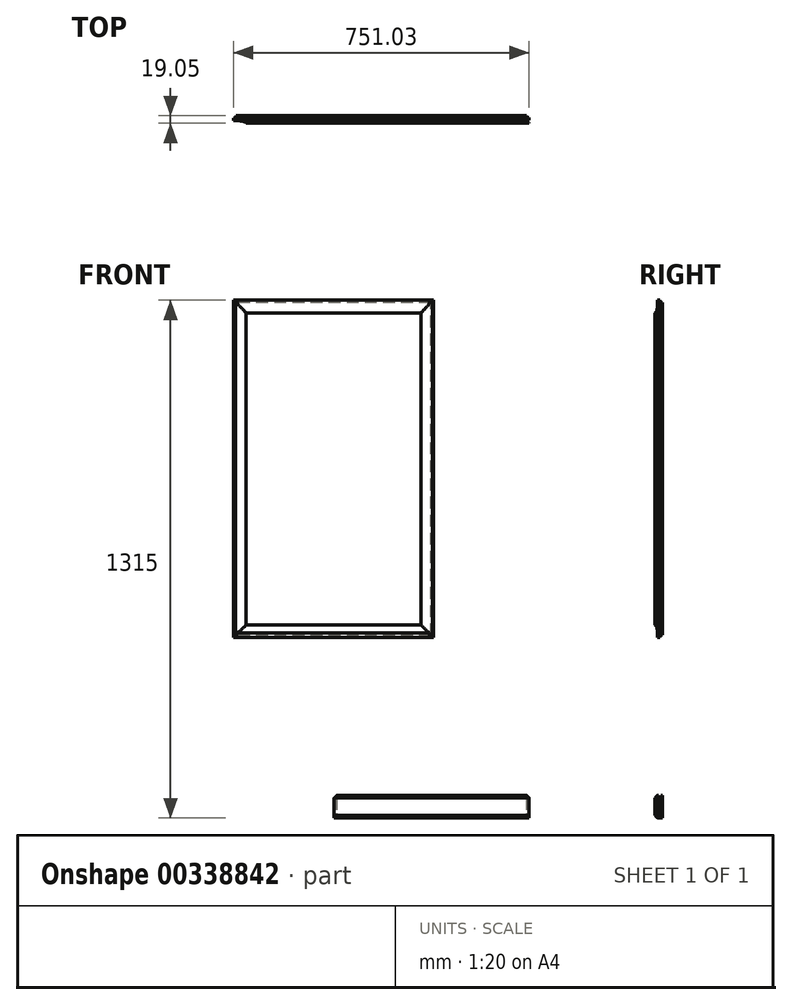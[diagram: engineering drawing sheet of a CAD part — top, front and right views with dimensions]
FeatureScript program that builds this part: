
annotation { "Feature Type Name" : "Feature", "Feature Type Description" : "" }
export const myFeature = defineFeature(function(context is Context, id is Id, definition is map)
    precondition{}
    {
        {
            var Q0;
            Q0=qCreatedBy(makeId("Front.planeOp"),FACE);
            var sketch = newSketch(context, id + "F0", { "sketchPlane" : qUnion([Q0])});
            skLineSegment(sketch, "E0.bottom", {"start": v(-252.27, 59.22) * mm, "end": v(243.03, 59.22) * mm});
            skLineSegment(sketch, "E0.top", {"start": v(-252.27, 2.07) * mm, "end": v(243.03, 2.07) * mm});
            skLineSegment(sketch, "E0.left", {"start": v(-252.27, 59.22) * mm, "end": v(-252.27, 2.07) * mm});
            skLineSegment(sketch, "E0.right", {"start": v(243.03, 59.22) * mm, "end": v(243.03, 2.07) * mm});
            skSolve(sketch);
        }
        {
            var Q0;
            Q0 = qSketchRegion(id + "F0", true);
            extrude(context, id + "F1", {"entities" : qUnion([Q0]), "depth" : 19.05 * mm});
        }
        {
            var Q0;
            Q0=makeQuery(id+"F1.opExtrude","SWEPT_FACE",FACE,{"disambiguationData":[OSD([sQuery(id+"F0.wireOp",EDGE,"E0.top")])]});
            var sketch = newSketch(context, id + "F2", { "sketchPlane" : qUnion([Q0])});
            skLineSegment(sketch, "E1.0", {"start": v(-252.27, 17.46) * mm, "end": v(243.03, 17.46) * mm, "construction": true});
            skLineSegment(sketch, "E2.0", {"start": v(-252.27, 11.11) * mm, "end": v(243.03, 11.11) * mm, "construction": true});
            skLineSegment(sketch, "E3.0", {"start": v(-252.27, 4.76) * mm, "end": v(243.03, 4.76) * mm, "construction": true});
            skLineSegment(sketch, "E4.0", {"start": v(236.68, 25.4) * mm, "end": v(236.68, 0) * mm, "construction": true});
            skArc(sketch, "E5", {"start": v(243.03, 17.46) * mm, "mid": v(238.54, 15.6) * mm, "end": v(236.68, 11.11) * mm});
            skLineSegment(sketch, "E6", {"start": v(236.68, 11.11) * mm, "end": v(243.03, 11.11) * mm});
            skLineSegment(sketch, "E7", {"start": v(243.03, 4.76) * mm, "end": v(236.68, 4.76) * mm});
            skLineSegment(sketch, "E8", {"start": v(236.68, 4.76) * mm, "end": v(236.68, 0) * mm});
            skLineSegment(sketch, "E9.0", {"start": v(-245.92, 19.05) * mm, "end": v(-245.92, 0) * mm, "construction": true});
            skArc(sketch, "E10", {"start": v(-245.92, 11.11) * mm, "mid": v(-247.78, 15.6) * mm, "end": v(-252.27, 17.46) * mm});
            skLineSegment(sketch, "E11", {"start": v(-245.92, 11.11) * mm, "end": v(-252.27, 11.11) * mm});
            skLineSegment(sketch, "E12", {"start": v(-252.27, 4.76) * mm, "end": v(-245.92, 4.76) * mm});
            skLineSegment(sketch, "E13", {"start": v(-245.92, 4.76) * mm, "end": v(-245.92, 0) * mm});
            skSolve(sketch);
        }
        {
            var Q0;
            {var subQ0=sQuery(id+"F2.wireOp",EDGE,"E5");Q0=makeQuery(id+"F2.imprint","IMPRINT",FACE,{"disambiguationData":[TD([[makeQuery(id+"F2.imprint","IMPRINT",EDGE,{"derivedFrom":subQ0}),1.0]])]});}
            var Q1;
            {var subQ0=sQuery(id+"F2.wireOp",EDGE,"E7");Q1=makeQuery(id+"F2.imprint","IMPRINT",FACE,{"disambiguationData":[TD([[makeQuery(id+"F2.imprint","IMPRINT",EDGE,{"derivedFrom":subQ0}),1.0]])]});}
            extrude(context, id + "F3", {"entities" : qUnion([Q0, Q1]), "operationType" : NewBodyOperationType.REMOVE, "oppositeDirection" : true, "depth" : 57.15 * mm});
        }
        {
            var Q0;
            {var subQ0=sQuery(id+"F2.wireOp",EDGE,"E10");Q0=makeQuery(id+"F2.imprint","IMPRINT",FACE,{"disambiguationData":[TD([[makeQuery(id+"F2.imprint","IMPRINT",EDGE,{"derivedFrom":subQ0}),1.0]])]});}
            var Q1;
            {var subQ0=sQuery(id+"F2.wireOp",EDGE,"E12");Q1=makeQuery(id+"F2.imprint","IMPRINT",FACE,{"disambiguationData":[TD([[makeQuery(id+"F2.imprint","IMPRINT",EDGE,{"derivedFrom":subQ0}),-1.0]])]});}
            extrude(context, id + "F4", {"entities" : qUnion([Q0, Q1]), "operationType" : NewBodyOperationType.REMOVE, "oppositeDirection" : true, "depth" : 57.15 * mm});
        }
        {
            var Q0;
            Q0=makeQuery(id+"F4.boolean.opBoolean","SPLIT",FACE,{"disambiguationData":[TD([makeQuery(id+"F4.opExtrude","SWEPT_FACE",FACE,{"disambiguationData":[OSD([sQuery(id+"F2.wireOp",EDGE,"E11")])]})])],"derivedFrom":makeQuery(id+"F1.opExtrude","SWEPT_FACE",FACE,{"disambiguationData":[OSD([sQuery(id+"F0.wireOp",EDGE,"E0.left")])]})});
            var sketch = newSketch(context, id + "F5", { "sketchPlane" : qUnion([Q0])});
            skLineSegment(sketch, "E14.0", {"start": v(11.11, 8.42) * mm, "end": v(4.76, 8.42) * mm, "construction": true});
            skLineSegment(sketch, "E15.0", {"start": v(19.05, 8.42) * mm, "end": v(17.46, 8.42) * mm, "construction": true});
            skLineSegment(sketch, "E16.0", {"start": v(11.11, 52.87) * mm, "end": v(4.76, 52.87) * mm, "construction": true});
            skLineSegment(sketch, "E17.0", {"start": v(19.05, 52.87) * mm, "end": v(17.46, 52.87) * mm, "construction": true});
            skArc(sketch, "E18", {"start": v(17.46, 52.87) * mm, "mid": v(15.6, 57.36) * mm, "end": v(11.11, 59.22) * mm});
            skArc(sketch, "E19", {"start": v(11.11, 2.07) * mm, "mid": v(15.6, 3.93) * mm, "end": v(17.46, 8.42) * mm});
            skLineSegment(sketch, "E20", {"start": v(19.05, 52.87) * mm, "end": v(17.46, 52.87) * mm});
            skLineSegment(sketch, "E21", {"start": v(11.11, 59.22) * mm, "end": v(11.11, 52.87) * mm});
            skLineSegment(sketch, "E22", {"start": v(4.76, 52.87) * mm, "end": v(11.11, 52.87) * mm});
            skLineSegment(sketch, "E23", {"start": v(4.76, 59.22) * mm, "end": v(4.76, 52.87) * mm});
            skLineSegment(sketch, "E24", {"start": v(11.11, 2.07) * mm, "end": v(11.11, 8.42) * mm});
            skLineSegment(sketch, "E25", {"start": v(19.05, 8.42) * mm, "end": v(17.46, 8.42) * mm});
            skLineSegment(sketch, "E26", {"start": v(19.05, 8.42) * mm, "end": v(19.05, 2.07) * mm});
            skLineSegment(sketch, "E27", {"start": v(19.05, 2.07) * mm, "end": v(11.11, 2.07) * mm});
            skLineSegment(sketch, "E28", {"start": v(19.05, 52.87) * mm, "end": v(19.05, 59.22) * mm});
            skLineSegment(sketch, "E29", {"start": v(11.11, 59.22) * mm, "end": v(19.05, 59.22) * mm});
            skSolve(sketch);
        }
        {
            var Q0;
            Q0=makeQuery(id+"F5.imprint","IMPRINT",FACE,{"disambiguationData":[TD([[makeQuery(id+"F5.imprint","IMPRINT",EDGE,{"derivedFrom":sQuery(id+"F5.wireOp",EDGE,"E18")}),-1.0]])]});
            var Q1;
            Q1=makeQuery(id+"F5.imprint","IMPRINT",FACE,{"disambiguationData":[TD([[makeQuery(id+"F5.imprint","IMPRINT",EDGE,{"derivedFrom":sQuery(id+"F5.wireOp",EDGE,"E19")}),-1.0]])]});
            var Q2;
            Q2=makeQuery(id+"F5.imprint","IMPRINT",FACE,{"disambiguationData":[TD([[makeQuery(id+"F5.imprint","IMPRINT",EDGE,{"derivedFrom":sQuery(id+"F5.wireOp",EDGE,"E21")}),-1.0]])]});
            extrude(context, id + "F6", {"entities" : qUnion([Q0, Q1, Q2]), "operationType" : NewBodyOperationType.REMOVE, "oppositeDirection" : true, "depth" : 495.3 * mm});
        }
        {
            var Q0;
            Q0=qCreatedBy(makeId("Front.planeOp"),FACE);
            var sketch = newSketch(context, id + "F7", { "sketchPlane" : qUnion([Q0])});
            skLineSegment(sketch, "E30.bottom", {"start": v(-508, 1317.07) * mm, "end": v(0, 1317.07) * mm});
            skLineSegment(sketch, "E30.top", {"start": v(-508, 459.82) * mm, "end": v(0, 459.82) * mm});
            skLineSegment(sketch, "E30.left", {"start": v(-508, 1317.07) * mm, "end": v(-508, 459.82) * mm});
            skLineSegment(sketch, "E30.right", {"start": v(0, 1317.07) * mm, "end": v(0, 459.82) * mm});
            skSolve(sketch);
        }
        {
            var Q0;
            Q0 = qSketchRegion(id + "F7", true);
            extrude(context, id + "F8", {"entities" : qUnion([Q0]), "depth" : 19.05 * mm});
        }
        {
            var Q0;
            Q0=makeQuery(id+"F8.opExtrude","SWEPT_FACE",FACE,{"disambiguationData":[OSD([sQuery(id+"F7.wireOp",EDGE,"E30.bottom")])]});
            var sketch = newSketch(context, id + "F9", { "sketchPlane" : qUnion([Q0])});
            skLineSegment(sketch, "E31.0", {"start": v(-501.65, -19.05) * mm, "end": v(-501.65, 0) * mm, "construction": true});
            skLineSegment(sketch, "E32.0", {"start": v(-508, -12.7) * mm, "end": v(0, -12.7) * mm, "construction": true});
            skLineSegment(sketch, "E33.0", {"start": v(-508, -6.35) * mm, "end": v(0, -6.35) * mm, "construction": true});
            skLineSegment(sketch, "E34.0", {"start": v(-476.25, -19.05) * mm, "end": v(-476.25, 0) * mm, "construction": true});
            skEllipticalArc(sketch, "E35", {});
            skLineSegment(sketch, "E36", {"start": v(-503.07, -12.7) * mm, "end": v(-508, -12.7) * mm});
            skLineSegment(sketch, "E37", {"start": v(-508, -6.35) * mm, "end": v(-508, -12.7) * mm});
            skLineSegment(sketch, "E38", {"start": v(-501.65, -6.35) * mm, "end": v(-508, -6.35) * mm});
            skLineSegment(sketch, "E39", {"start": v(-501.65, 0) * mm, "end": v(-501.65, -6.35) * mm});
            skLineSegment(sketch, "E40.0", {"start": v(-6.35, -19.05) * mm, "end": v(-6.35, 0) * mm, "construction": true});
            skLineSegment(sketch, "E41.0", {"start": v(-31.75, -19.05) * mm, "end": v(-31.75, 0) * mm, "construction": true});
            skEllipticalArc(sketch, "E42", {});
            skLineSegment(sketch, "E43", {"start": v(-2.95, -12.7) * mm, "end": v(0, -12.7) * mm});
            skLineSegment(sketch, "E44", {"start": v(0, -12.7) * mm, "end": v(0, -6.35) * mm});
            skLineSegment(sketch, "E45", {"start": v(0, -6.35) * mm, "end": v(-6.35, -6.35) * mm});
            skLineSegment(sketch, "E46", {"start": v(-6.35, -6.35) * mm, "end": v(-6.35, 0) * mm});
            const initialGuessF9  = {"E35": [-0.50165, -0.01905, 1, 0, 0.0254, 0.0063599247448927225, 0, 1.6266697369398573], "E42": [-0.00635, -0.01905, -1, 0, 0.0254, 0.0064077341289209755, 4.578048873305623, 0]};
            skSetInitialGuess(sketch, initialGuessF9);
            skSolve(sketch);
        }
        {
            var Q0;
            {var subQ0=sQuery(id+"F9.wireOp",EDGE,"E35");Q0=makeQuery(id+"F9.imprint","IMPRINT",FACE,{"disambiguationData":[TD([[makeQuery(id+"F9.imprint","IMPRINT",EDGE,{"derivedFrom":subQ0}),1.0]])]});}
            var Q1;
            {var subQ0=sQuery(id+"F9.wireOp",EDGE,"E38");Q1=makeQuery(id+"F9.imprint","IMPRINT",FACE,{"disambiguationData":[TD([[makeQuery(id+"F9.imprint","IMPRINT",EDGE,{"derivedFrom":subQ0}),-1.0]])]});}
            extrude(context, id + "F10", {"entities" : qUnion([Q0, Q1]), "operationType" : NewBodyOperationType.REMOVE, "oppositeDirection" : true, "depth" : 863.6 * mm});
        }
        {
            var Q0;
            {var subQ0=sQuery(id+"F9.wireOp",EDGE,"E45");Q0=makeQuery(id+"F9.imprint","IMPRINT",FACE,{"disambiguationData":[TD([[makeQuery(id+"F9.imprint","IMPRINT",EDGE,{"derivedFrom":subQ0}),-1.0]])]});}
            var Q1;
            {var subQ0=sQuery(id+"F9.wireOp",EDGE,"E42");Q1=makeQuery(id+"F9.imprint","IMPRINT",FACE,{"disambiguationData":[TD([[makeQuery(id+"F9.imprint","IMPRINT",EDGE,{"derivedFrom":subQ0}),1.0]])]});}
            extrude(context, id + "F11", {"entities" : qUnion([Q0, Q1]), "operationType" : NewBodyOperationType.REMOVE, "oppositeDirection" : true, "depth" : 965.2 * mm});
        }
        {
            var Q0;
            Q0=makeQuery(id+"F8.opExtrude","SWEPT_FACE",FACE,{"disambiguationData":[OSD([sQuery(id+"F7.wireOp",EDGE,"E30.left")])]});
            var sketch = newSketch(context, id + "F12", { "sketchPlane" : qUnion([Q0])});
            skLineSegment(sketch, "E47.0", {"start": v(22.42, 1310.72) * mm, "end": v(-2.22, 1310.72) * mm, "construction": true});
            skLineSegment(sketch, "E48.0", {"start": v(23.6, 1285.32) * mm, "end": v(-3.13, 1285.32) * mm, "construction": true});
            skLineSegment(sketch, "E49", {"start": v(0, 1310.72) * mm, "end": v(6.35, 1310.72) * mm});
            skLineSegment(sketch, "E50", {"start": v(6.35, 1310.72) * mm, "end": v(6.35, 1317.07) * mm});
            skLineSegment(sketch, "E51", {"start": v(0, 1310.72) * mm, "end": v(0, 1317.07) * mm});
            skLineSegment(sketch, "E52", {"start": v(6.35, 1317.07) * mm, "end": v(0, 1317.07) * mm});
            skLineSegment(sketch, "E53.0", {"start": v(19.05, 459.82) * mm, "end": v(19.05, 1317.07) * mm, "construction": true});
            skLineSegment(sketch, "E54.0", {"start": v(0, 459.82) * mm, "end": v(0, 1317.07) * mm, "construction": true});
            skEllipticalArc(sketch, "E55", {});
            skLineSegment(sketch, "E56", {"start": v(19.3, 1285.32) * mm, "end": v(19.05, 1317.07) * mm});
            skLineSegment(sketch, "E57", {"start": v(19.05, 1317.07) * mm, "end": v(12.7, 1317.07) * mm});
            skLineSegment(sketch, "E58", {"start": v(12.7, 1317.07) * mm, "end": v(12.74, 1310.72) * mm});
            skLineSegment(sketch, "E59.0", {"start": v(19.05, 466.17) * mm, "end": v(0, 466.17) * mm, "construction": true});
            skLineSegment(sketch, "E60.0", {"start": v(19.05, 491.57) * mm, "end": v(0, 491.57) * mm, "construction": true});
            skEllipticalArc(sketch, "E61", {});
            skLineSegment(sketch, "E62", {"start": v(19.05, 491.57) * mm, "end": v(19.05, 459.82) * mm});
            skLineSegment(sketch, "E63", {"start": v(12.7, 459.82) * mm, "end": v(19.05, 459.82) * mm});
            skLineSegment(sketch, "E64", {"start": v(12.7, 459.82) * mm, "end": v(12.54, 466.17) * mm});
            skLineSegment(sketch, "E65", {"start": v(6.35, 459.82) * mm, "end": v(6.35, 466.17) * mm});
            skLineSegment(sketch, "E66", {"start": v(6.35, 466.17) * mm, "end": v(0, 466.17) * mm});
            skLineSegment(sketch, "E67", {"start": v(0, 459.82) * mm, "end": v(0, 466.17) * mm});
            skLineSegment(sketch, "E68", {"start": v(0, 459.82) * mm, "end": v(6.35, 459.82) * mm});
            const initialGuessF12  = {"E55": [0.01905, 1.3107178656908895, 0, -1, 0.025421544775667382, 0.006310914746219019, 4.71238898038469, 0.041173301652699494], "E61": [0.01905, 0.46616787632435824, 0, 1, 0.0254, 0.006512066739909608, 0, 1.5707963267948966]};
            skSetInitialGuess(sketch, initialGuessF12);
            skSolve(sketch);
        }
        {
            var Q0;
            Q0=makeQuery(id+"F12.imprint","IMPRINT",FACE,{"disambiguationData":[TD([[makeQuery(id+"F12.imprint","IMPRINT",EDGE,{"derivedFrom":sQuery(id+"F12.wireOp",EDGE,"E55")}),1.0]])]});
            var Q1;
            Q1=makeQuery(id+"F12.imprint","IMPRINT",FACE,{"disambiguationData":[TD([[makeQuery(id+"F12.imprint","IMPRINT",EDGE,{"derivedFrom":sQuery(id+"F12.wireOp",EDGE,"E49")}),1.0]])]});
            extrude(context, id + "F13", {"entities" : qUnion([Q0, Q1]), "operationType" : NewBodyOperationType.REMOVE, "oppositeDirection" : true, "depth" : 508 * mm});
        }
        {
            var Q0;
            Q0=makeQuery(id+"F12.imprint","IMPRINT",FACE,{"disambiguationData":[TD([[makeQuery(id+"F12.imprint","IMPRINT",EDGE,{"derivedFrom":sQuery(id+"F12.wireOp",EDGE,"E65")}),1.0]])]});
            var Q1;
            {var subQ0=sQuery(id+"F12.wireOp",EDGE,"E62");Q1=makeQuery(id+"F12.imprint","IMPRINT",FACE,{"disambiguationData":[TD([[makeQuery(id+"F12.imprint","IMPRINT",EDGE,{"derivedFrom":subQ0}),-1.0]])]});}
            extrude(context, id + "F14", {"entities" : qUnion([Q0, Q1]), "operationType" : NewBodyOperationType.REMOVE, "oppositeDirection" : true, "depth" : 508 * mm});
        }
    });
